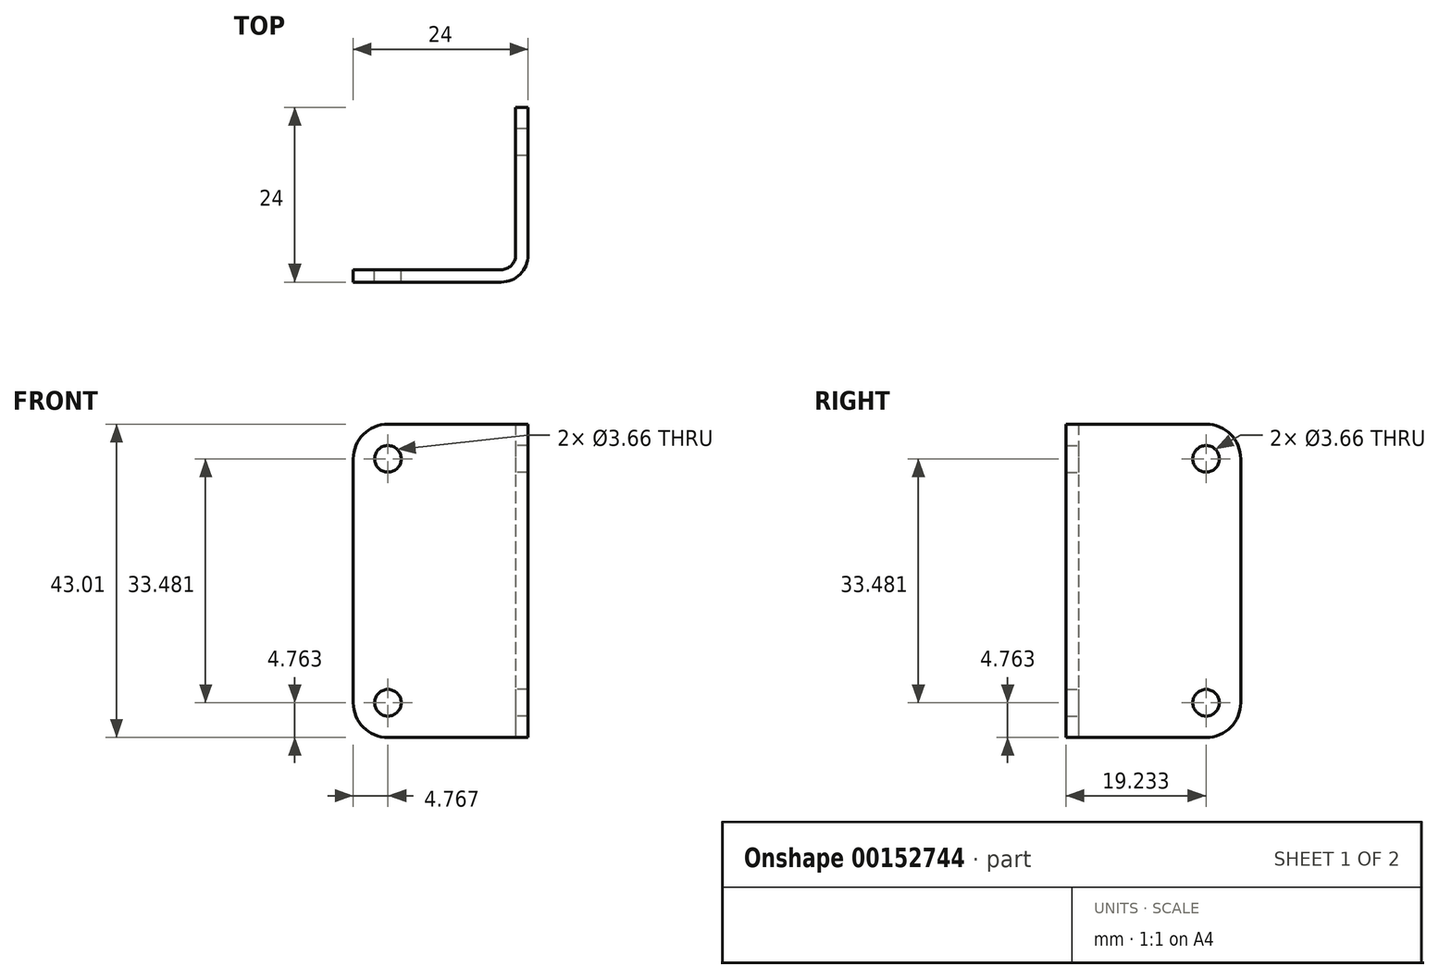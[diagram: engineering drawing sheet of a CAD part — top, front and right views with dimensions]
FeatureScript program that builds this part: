
annotation { "Feature Type Name" : "Feature", "Feature Type Description" : "" }
export const myFeature = defineFeature(function(context is Context, id is Id, definition is map)
    precondition{}
    {
        {
            var Q0;
            Q0=qCreatedBy(makeId("Top.planeOp"),FACE);
            var sketch = newSketch(context, id + "F0", { "sketchPlane" : qUnion([Q0])});
            skLineSegment(sketch, "E0.top", {"start": v(0, 22.29) * mm, "end": v(1.7, 22.29) * mm});
            skLineSegment(sketch, "E0.left", {"start": v(0, 0) * mm, "end": v(0, 22.29) * mm});
            skLineSegment(sketch, "E0.right", {"start": v(1.7, -1.7) * mm, "end": v(1.7, 22.29) * mm});
            skLineSegment(sketch, "E1.bottom", {"start": v(0, 0) * mm, "end": v(-22.29, 0) * mm});
            skLineSegment(sketch, "E1.top", {"start": v(1.7, -1.7) * mm, "end": v(-22.29, -1.7) * mm});
            skLineSegment(sketch, "E1.right", {"start": v(-22.29, 0) * mm, "end": v(-22.29, -1.7) * mm});
            skSolve(sketch);
        }
        {
            var Q0;
            Q0 = qSketchRegion(id + "F0", true);
            extrude(context, id + "F1", {"entities" : qUnion([Q0]), "depth" : 43 * mm});
        }
        {
            var Q0;
            Q0=makeQuery(id+"F1.opExtrude","SWEPT_EDGE",EDGE,{"disambiguationData":[OSD([sQuery(id+"F0.wireOp",EDGE,"E0.left"),sQuery(id+"F0.wireOp",EDGE,"E1.bottom")])]});
            fillet(context, id + "F2", {"entities" : qUnion([Q0]), "radius" : 1.98 * mm, "tangentPropagation" : true, "allowEdgeOverflow" : false});
        }
        {
            var Q0;
            Q0=makeQuery(id+"F1.opExtrude","SWEPT_EDGE",EDGE,{"disambiguationData":[OSD([sQuery(id+"F0.wireOp",EDGE,"E0.right"),sQuery(id+"F0.wireOp",EDGE,"E1.top")])]});
            fillet(context, id + "F3", {"entities" : qUnion([Q0]), "radius" : 3.7 * mm, "tangentPropagation" : true, "allowEdgeOverflow" : false});
        }
        {
            var Q0;
            Q0=makeQuery(id+"F1.opExtrude","SWEPT_FACE",FACE,{"disambiguationData":[OSD([sQuery(id+"F0.wireOp",EDGE,"E0.left")])]});
            var sketch = newSketch(context, id + "F4", { "sketchPlane" : qUnion([Q0])});
            skLineSegment(sketch, "E2", {"start": v(-22.29, 21.5) * mm, "end": v(-17.52, 21.5) * mm, "construction": true});
            skLineSegment(sketch, "E3", {"start": v(-17.52, 38.24) * mm, "end": v(-17.52, 4.76) * mm, "construction": true});
            skLineSegment(sketch, "E4", {"start": v(-17.52, 4.76) * mm, "end": v(-17.52, 0) * mm, "construction": true});
            skCircle(sketch, "E5", {"center": v(-17.52, 38.24) * mm, "radius": 1.83 * mm});
            skCircle(sketch, "E6", {"center": v(-17.52, 4.76) * mm, "radius": 1.83 * mm});
            skSolve(sketch);
        }
        {
            var Q0;
            Q0 = qSketchRegion(id + "F4", true);
            var Q1;
            Q1=makeQuery(id+"F1.opExtrude","SWEPT_FACE",FACE,{"disambiguationData":[OSD([sQuery(id+"F0.wireOp",EDGE,"E0.right")])]});
            extrude(context, id + "F5", {"entities" : qUnion([Q0]), "operationType" : NewBodyOperationType.REMOVE, "endBound" : BoundingType.UP_TO_SURFACE, "oppositeDirection" : true, "endBoundEntityFace" : qUnion([Q1]), "depth" : 25.4 * mm});
        }
        {
            var Q0;
            Q0=makeQuery(id+"F1.opExtrude","SWEPT_FACE",FACE,{"disambiguationData":[OSD([sQuery(id+"F0.wireOp",EDGE,"E1.bottom")])]});
            var sketch = newSketch(context, id + "F6", { "sketchPlane" : qUnion([Q0])});
            skLineSegment(sketch, "E7", {"start": v(22.29, 21.5) * mm, "end": v(17.52, 21.5) * mm, "construction": true});
            skLineSegment(sketch, "E8", {"start": v(17.52, 38.24) * mm, "end": v(17.52, 4.76) * mm, "construction": true});
            skLineSegment(sketch, "E9", {"start": v(17.52, 4.76) * mm, "end": v(17.52, 0) * mm, "construction": true});
            skCircle(sketch, "E10", {"center": v(17.52, 38.24) * mm, "radius": 1.83 * mm});
            skCircle(sketch, "E11", {"center": v(17.52, 4.76) * mm, "radius": 1.83 * mm});
            skSolve(sketch);
        }
        {
            var Q0;
            Q0 = qSketchRegion(id + "F6", true);
            var Q1;
            Q1=makeQuery(id+"F1.opExtrude","SWEPT_FACE",FACE,{"disambiguationData":[OSD([sQuery(id+"F0.wireOp",EDGE,"E1.top")])]});
            extrude(context, id + "F7", {"entities" : qUnion([Q0]), "operationType" : NewBodyOperationType.REMOVE, "endBound" : BoundingType.UP_TO_SURFACE, "oppositeDirection" : true, "endBoundEntityFace" : qUnion([Q1]), "depth" : 25.4 * mm});
        }
        {
            var Q0;
            Q0=makeQuery(id+"F1.opExtrude","CAP_EDGE",EDGE,{"disambiguationData":[OSD([sQuery(id+"F0.wireOp",EDGE,"E0.top")])],"isStart":false});
            var Q1;
            Q1=makeQuery(id+"F1.opExtrude","CAP_EDGE",EDGE,{"disambiguationData":[OSD([sQuery(id+"F0.wireOp",EDGE,"E1.right")])],"isStart":false});
            var Q2;
            Q2=makeQuery(id+"F1.opExtrude","CAP_EDGE",EDGE,{"disambiguationData":[OSD([sQuery(id+"F0.wireOp",EDGE,"E1.right")])],"isStart":true});
            var Q3;
            Q3=makeQuery(id+"F1.opExtrude","CAP_EDGE",EDGE,{"disambiguationData":[OSD([sQuery(id+"F0.wireOp",EDGE,"E0.top")])],"isStart":true});
            fillet(context, id + "F8", {"entities" : qUnion([Q0, Q1, Q2, Q3]), "radius" : 4.76 * mm, "tangentPropagation" : true, "allowEdgeOverflow" : false});
        }
    });
